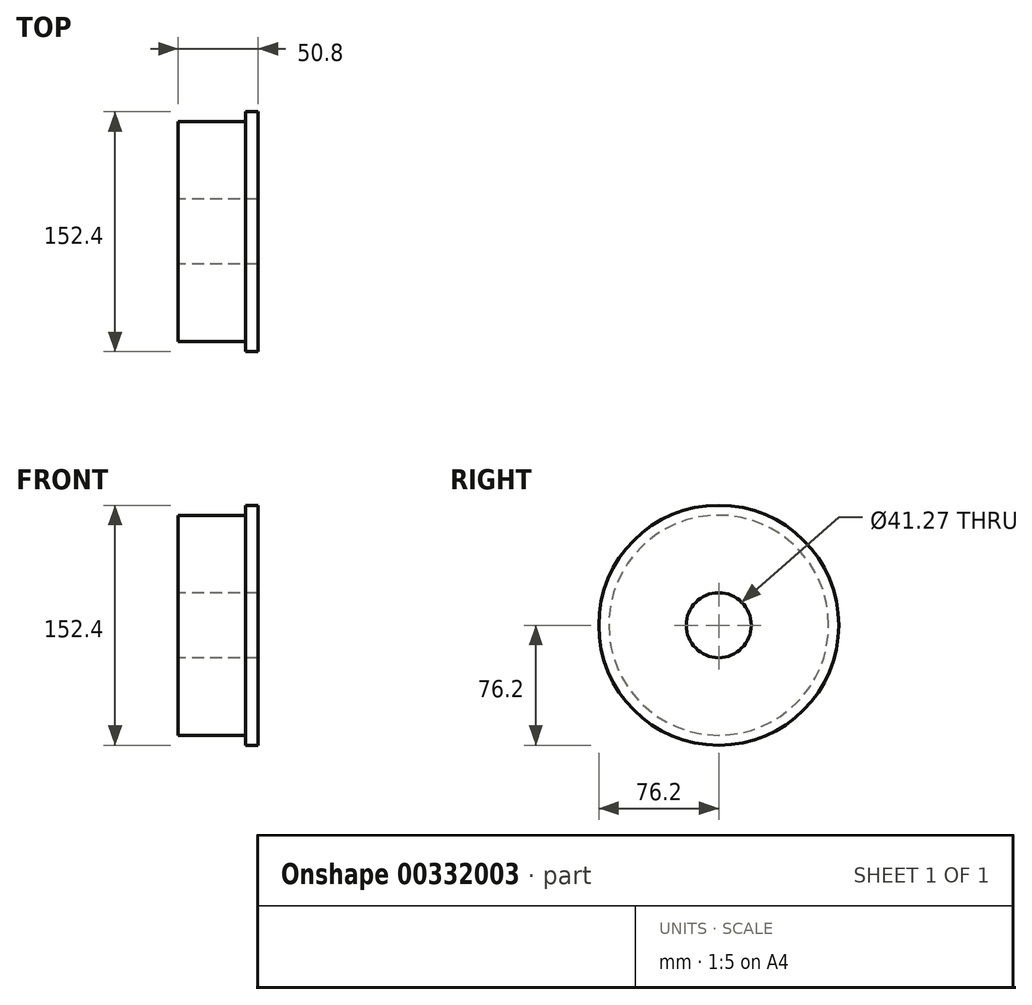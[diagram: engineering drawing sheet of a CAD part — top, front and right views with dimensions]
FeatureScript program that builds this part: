
annotation { "Feature Type Name" : "Feature", "Feature Type Description" : "" }
export const myFeature = defineFeature(function(context is Context, id is Id, definition is map)
    precondition{}
    {
        {
            var Q0;
            Q0=qCreatedBy(makeId("Right.planeOp"),FACE);
            var sketch = newSketch(context, id + "F0", { "sketchPlane" : qUnion([Q0])});
            skCircle(sketch, "E0", {"center": v(0, 0) * mm, "radius": 69.85 * mm});
            skCircle(sketch, "E1", {"center": v(0, 0) * mm, "radius": 20.64 * mm});
            skSolve(sketch);
        }
        {
            var Q0;
            Q0 = qSketchRegion(id + "F0", true);
            extrude(context, id + "F1", {"entities" : qUnion([Q0]), "depth" : 42.93 * mm});
        }
        {
            var Q0;
            Q0=makeQuery(id+"F1.opExtrude","CAP_FACE",FACE,{"disambiguationData":[OSD([sQuery(id+"F0.wireOp",EDGE,"E0"),sQuery(id+"F0.wireOp",EDGE,"E1")])],"isStart":false});
            var sketch = newSketch(context, id + "F2", { "sketchPlane" : qUnion([Q0])});
            skCircle(sketch, "E2", {"center": v(0, 0) * mm, "radius": 76.2 * mm});
            skCircle(sketch, "E3.0", {"center": v(0, 0) * mm, "radius": 20.64 * mm});
            skSolve(sketch);
        }
        {
            var Q0;
            Q0 = qSketchRegion(id + "F2", true);
            extrude(context, id + "F3", {"entities" : qUnion([Q0]), "operationType" : NewBodyOperationType.ADD, "depth" : 7.87 * mm});
        }
    });
